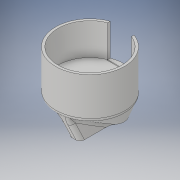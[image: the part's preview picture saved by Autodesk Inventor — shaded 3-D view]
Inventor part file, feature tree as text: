
AUTODESK INVENTOR PART (.ipt)
format: ipt  version: 2019 (Build 230136000, 136)  size: 462,848 bytes
history: native  units: mm
features: sketch x7, extrude x5, fillet x5, loft x2, other x2, plane x1
ambient origin geometry x8: Origin, YZ Plane, XZ Plane, XY Plane, X Axis, Y Axis, Z Axis, Center Point
bodies: Solid1 (feature_tree)
feature tree (22):
  extrude  "Extrusion1"  Depth=86.0mm
  extrude  "Extrusion2"  Depth=1.0mm
  extrude  "Extrusion3"  Depth=30.0mm
  sketch  "Sketch9"  dims[d7=80.0mm d8=10.0mm d9=0.0mm]
  plane  "Work Plane2"
  loft  "Loft1"
  extrude  "Extrusion6"  Depth=40.0mm
  loft  "Loft2"
  fillet  "Fillet1"  [1 undecoded]
  fillet  "Fillet2"  Radius=20.0mm
  extrude  "Extrusion8"  TaperAngle=0.0deg  [1 undecoded]
  fillet  "Fillet4"  [1 undecoded]
  fillet  "Fillet5"  Radius=10.0mm
  fillet  "Fillet6"  Radius=10.0mm
  sketch  "Sketch1"  dims[d0=80.0mm d1=86.0mm]
  sketch  "Sketch2"  dims[d2=40.0mm d3=0.0mm d4=1.0mm]
  sketch  "Sketch3"  dims[d5=1.0mm d6=30.0mm]
  sketch  "Sketch10"  dims[d10=10.0mm d11=0.0mm d21=40.0mm]
  sketch  "Sketch11"  dims[d22=26.0mm d23=0.0mm d24=90.0deg d25=0.0mm d26=90.0deg d27=20.0mm]
  other  "Edges1"
  other  "Edges2"
  sketch  "Sketch12"  dims[d28=20.0mm d29=0.0mm d30=0.0mm d31=90.0deg d32=0.0mm d33=90.0deg d34=10.0mm d35=10.0mm d36=86.0mm d37=86.0mm d38=43.0mm d39=86.0mm d43=15.0mm d44=0.0mm d45=5.0mm d46=2.0mm d47=2.0mm]
note: 3 required parameter values undecoded (feature->parameter linkage not recoverable at this tier; creation-order binding heuristic only, values carry confidence <= 0.55)
